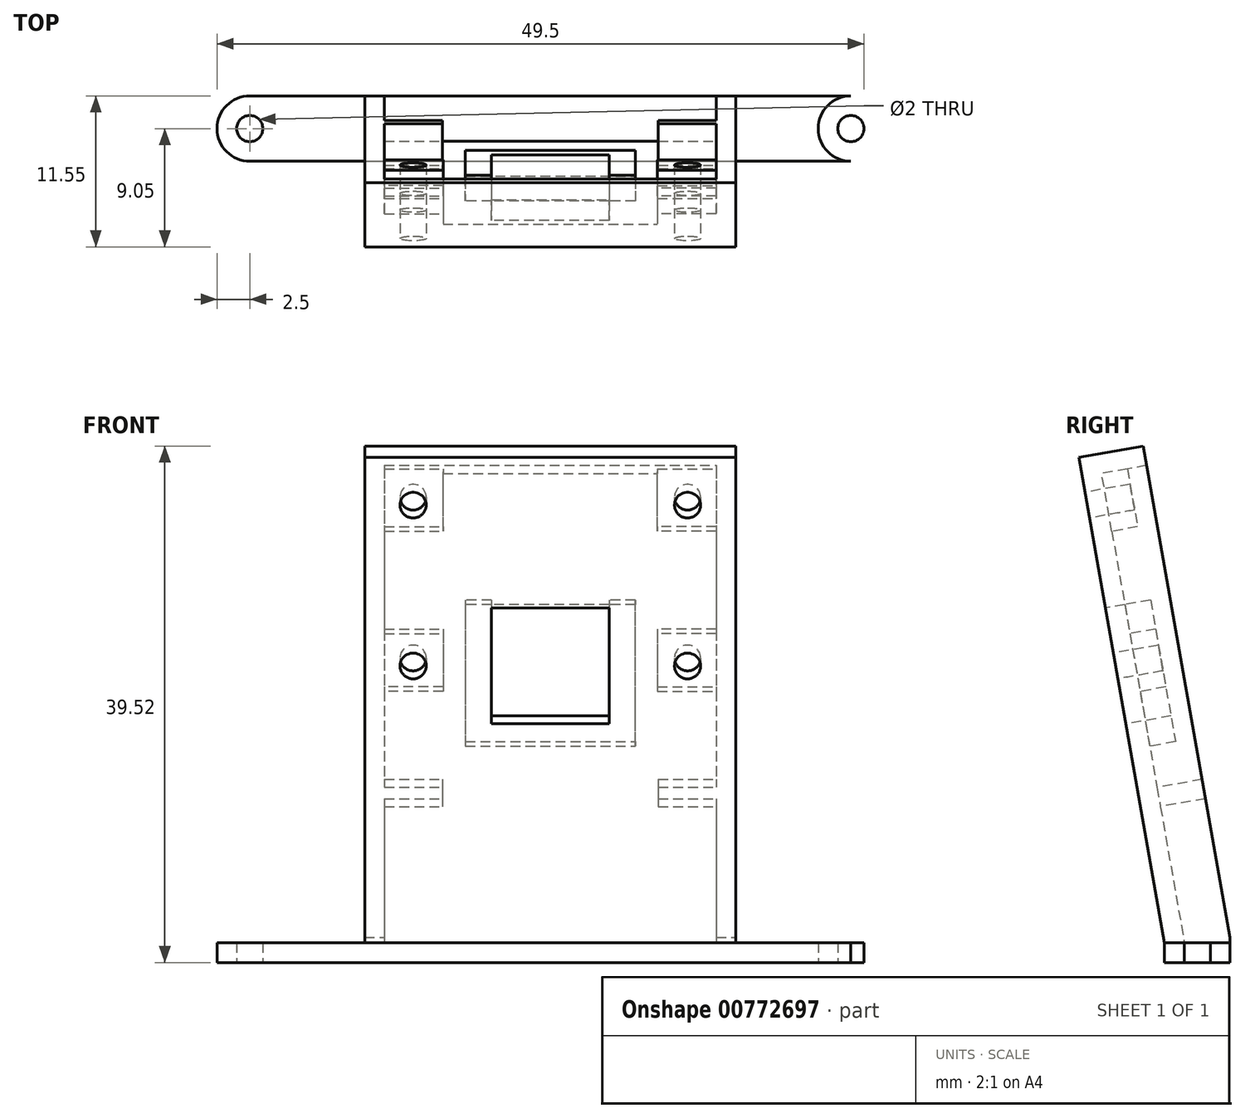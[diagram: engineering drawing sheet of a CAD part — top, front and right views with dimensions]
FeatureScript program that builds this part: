
annotation { "Feature Type Name" : "Feature", "Feature Type Description" : "" }
export const myFeature = defineFeature(function(context is Context, id is Id, definition is map)
    precondition{}
    {
        {
            var Q0;
            Q0=qCreatedBy(makeId("Top.planeOp"),FACE);
            var sketch = newSketch(context, id + "F0", { "sketchPlane" : qUnion([Q0])});
            skLineSegment(sketch, "E0.bottom", {"start": v(-23, 2.5) * mm, "end": v(23, 2.5) * mm});
            skLineSegment(sketch, "E0.top", {"start": v(-23, -2.5) * mm, "end": v(23, -2.5) * mm});
            skCircle(sketch, "E1", {"center": v(-23, 0) * mm, "radius": 2.5 * mm});
            skCircle(sketch, "E2.MirrorC", {"center": v(23, 0) * mm, "radius": 2.5 * mm});
            skCircle(sketch, "E3", {"center": v(-23, 0) * mm, "radius": 1 * mm});
            skCircle(sketch, "E4.MirrorC", {"center": v(23, 0) * mm, "radius": 1 * mm});
            skSolve(sketch);
        }
        {
            var Q0;
            Q0=makeQuery(id+"F0.imprint","IMPRINT",FACE,{"disambiguationData":[TD([[makeQuery(id+"F0.imprint","IMPRINT",EDGE,{"derivedFrom":sQuery(id+"F0.wireOp",EDGE,"E3")}),-1.0]])]});
            var Q1;
            {var subQ0=sQuery(id+"F0.wireOp",EDGE,"E0.bottom");Q1=makeQuery(id+"F0.imprint","IMPRINT",FACE,{"disambiguationData":[TD([[makeQuery(id+"F0.imprint","IMPRINT",EDGE,{"derivedFrom":subQ0}),-1.0]])]});}
            var Q2;
            Q2=makeQuery(id+"F0.imprint","IMPRINT",FACE,{"disambiguationData":[TD([[makeQuery(id+"F0.imprint","IMPRINT",EDGE,{"derivedFrom":sQuery(id+"F0.wireOp",EDGE,"E4.MirrorC")}),1.0]])]});
            extrude(context, id + "F1", {"entities" : qUnion([Q0, Q1, Q2]), "depth" : 1.5 * mm, "offsetDistance" : 25 * mm});
        }
        {
            var Q0;
            Q0=qCreatedBy(makeId("Front.planeOp"),FACE);
            var Q1;
            Q1=makeQuery(id+"F1.opExtrude","CAP_EDGE",EDGE,{"disambiguationData":[OSD([sQuery(id+"F0.wireOp",EDGE,"E0.top")])],"isStart":false});
            cPlane(context, id + "F2", {"entities" : qUnion([Q0, Q1]), "cplaneType" : CPlaneType.LINE_ANGLE, "offset" : 25 * mm, "angle" : 190 * degree, "width" : 150 * mm, "height" : 150 * mm});
        }
        {
            var Q0;
            Q0=qCreatedBy(id+"F2.planeOp",FACE);
            var sketch = newSketch(context, id + "F3", { "sketchPlane" : qUnion([Q0])});
            skLineSegment(sketch, "E5.bottom", {"start": v(-12.5, 37.93) * mm, "end": v(12.5, 37.93) * mm, "construction": true});
            skLineSegment(sketch, "E5.top", {"start": v(-12.5, 13.93) * mm, "end": v(12.5, 13.93) * mm, "construction": true});
            skLineSegment(sketch, "E5.left", {"start": v(-12.5, 37.93) * mm, "end": v(-12.5, 13.93) * mm, "construction": true});
            skLineSegment(sketch, "E5.right", {"start": v(12.5, 37.93) * mm, "end": v(12.5, 13.93) * mm, "construction": true});
            skLineSegment(sketch, "E6.bottom", {"start": v(-4.5, 27.93) * mm, "end": v(4.5, 27.93) * mm});
            skLineSegment(sketch, "E6.top", {"start": v(-4.5, 18.93) * mm, "end": v(4.5, 18.93) * mm});
            skLineSegment(sketch, "E6.left", {"start": v(-4.5, 27.93) * mm, "end": v(-4.5, 18.93) * mm});
            skLineSegment(sketch, "E6.right", {"start": v(4.5, 27.93) * mm, "end": v(4.5, 18.93) * mm});
            skLineSegment(sketch, "E7", {"start": v(-16.59, 23.43) * mm, "end": v(16.18, 23.43) * mm, "construction": true});
            skCircle(sketch, "E8", {"center": v(10.5, 23.43) * mm, "radius": 1 * mm});
            skCircle(sketch, "E9", {"center": v(-10.5, 23.43) * mm, "radius": 1 * mm});
            skCircle(sketch, "E10", {"center": v(-10.5, 35.93) * mm, "radius": 1 * mm});
            skCircle(sketch, "E11", {"center": v(10.5, 35.93) * mm, "radius": 1 * mm});
            skLineSegment(sketch, "E12", {"start": v(-4.5, 27.93) * mm, "end": v(-6.5, 27.93) * mm});
            skLineSegment(sketch, "E13", {"start": v(-6.5, 27.93) * mm, "end": v(-6.5, 16.93) * mm});
            skLineSegment(sketch, "E14", {"start": v(-6.5, 16.93) * mm, "end": v(6.5, 16.93) * mm});
            skLineSegment(sketch, "E15", {"start": v(6.5, 16.93) * mm, "end": v(6.5, 27.93) * mm});
            skLineSegment(sketch, "E16", {"start": v(6.5, 27.93) * mm, "end": v(4.5, 27.93) * mm});
            skLineSegment(sketch, "E17.bottom", {"start": v(-12.7, 38.13) * mm, "end": v(12.7, 38.13) * mm});
            skLineSegment(sketch, "E17.left", {"start": v(-12.7, 38.13) * mm, "end": v(-12.7, 13.73) * mm});
            skLineSegment(sketch, "E17.right", {"start": v(12.7, 38.13) * mm, "end": v(12.7, 13.73) * mm});
            skLineSegment(sketch, "E18.bottom", {"start": v(-14.2, 39.63) * mm, "end": v(14.2, 39.63) * mm});
            skLineSegment(sketch, "E18.left", {"start": v(-14.2, 39.63) * mm, "end": v(-14.2, 0.43) * mm});
            skLineSegment(sketch, "E18.right", {"start": v(14.2, 39.63) * mm, "end": v(14.2, 0.43) * mm});
            skLineSegment(sketch, "E19", {"start": v(-12.7, 13.73) * mm, "end": v(-8.25, 13.73) * mm});
            skLineSegment(sketch, "E20", {"start": v(-12.7, 12.23) * mm, "end": v(-8.25, 12.23) * mm});
            skLineSegment(sketch, "E21.trimOffspring", {"start": v(-12.7, 12.23) * mm, "end": v(-12.7, 0.43) * mm});
            skLineSegment(sketch, "E22.trimOffspring", {"start": v(12.7, 12.23) * mm, "end": v(12.7, 0.43) * mm});
            skLineSegment(sketch, "E23", {"start": v(-12.7, 33.63) * mm, "end": v(-8.2, 33.63) * mm});
            skLineSegment(sketch, "E24", {"start": v(-8.2, 33.63) * mm, "end": v(-8.2, 38.13) * mm});
            skLineSegment(sketch, "E25", {"start": v(-12.7, 25.68) * mm, "end": v(-8.2, 25.68) * mm});
            skLineSegment(sketch, "E26", {"start": v(-8.2, 25.68) * mm, "end": v(-8.2, 21.18) * mm});
            skLineSegment(sketch, "E27", {"start": v(-8.2, 21.18) * mm, "end": v(-12.7, 21.18) * mm});
            skLineSegment(sketch, "E28.MirrorCS", {"start": v(8.2, 33.63) * mm, "end": v(8.2, 38.13) * mm});
            skLineSegment(sketch, "E29.MirrorCS", {"start": v(12.7, 33.63) * mm, "end": v(8.2, 33.63) * mm});
            skLineSegment(sketch, "E30.MirrorCS", {"start": v(8.2, 21.18) * mm, "end": v(12.7, 21.18) * mm});
            skLineSegment(sketch, "E31.MirrorCS", {"start": v(12.7, 25.68) * mm, "end": v(8.2, 25.68) * mm});
            skLineSegment(sketch, "E32.MirrorCS", {"start": v(8.2, 25.68) * mm, "end": v(8.2, 21.18) * mm});
            skLineSegment(sketch, "E33", {"start": v(8.25, 13.73) * mm, "end": v(8.25, 12.23) * mm});
            skLineSegment(sketch, "E34", {"start": v(-8.25, 13.73) * mm, "end": v(-8.25, 12.23) * mm});
            skLineSegment(sketch, "E35.trimOffspring", {"start": v(8.25, 12.23) * mm, "end": v(12.7, 12.23) * mm});
            skLineSegment(sketch, "E36.trimOffspring", {"start": v(8.25, 13.73) * mm, "end": v(12.7, 13.73) * mm});
            skLineSegment(sketch, "E37", {"start": v(-14.2, 0.43) * mm, "end": v(14.2, 0.43) * mm});
            skSolve(sketch);
        }
        {
            var Q0;
            Q0=makeQuery(id+"F3.imprint","IMPRINT",FACE,{"disambiguationData":[TD([[makeQuery(id+"F3.imprint","IMPRINT",EDGE,{"derivedFrom":sQuery(id+"F3.wireOp",EDGE,"E6.bottom")}),1.0]])]});
            extrude(context, id + "F4", {"entities" : qUnion([Q0]), "operationType" : NewBodyOperationType.ADD, "oppositeDirection" : true, "depth" : 1.5 * mm, "offsetDistance" : 25 * mm});
        }
        {
            var Q0;
            Q0=makeQuery(id+"F3.imprint","IMPRINT",FACE,{"disambiguationData":[TD([[makeQuery(id+"F3.imprint","IMPRINT",EDGE,{"derivedFrom":sQuery(id+"F3.wireOp",EDGE,"E18.bottom")}),-1.0]])]});
            extrude(context, id + "F5", {"entities" : qUnion([Q0]), "operationType" : NewBodyOperationType.ADD, "oppositeDirection" : true, "depth" : 5 * mm, "offsetDistance" : 25 * mm});
        }
        {
            var Q0;
            Q0=makeQuery(id+"F3.imprint","IMPRINT",FACE,{"disambiguationData":[TD([[makeQuery(id+"F3.imprint","IMPRINT",EDGE,{"derivedFrom":sQuery(id+"F3.wireOp",EDGE,"E10")}),-1.0]])]});
            var Q1;
            Q1=makeQuery(id+"F3.imprint","IMPRINT",FACE,{"disambiguationData":[TD([[makeQuery(id+"F3.imprint","IMPRINT",EDGE,{"derivedFrom":sQuery(id+"F3.wireOp",EDGE,"E11")}),-1.0]])]});
            var Q2;
            Q2=makeQuery(id+"F3.imprint","IMPRINT",FACE,{"disambiguationData":[TD([[makeQuery(id+"F3.imprint","IMPRINT",EDGE,{"derivedFrom":sQuery(id+"F3.wireOp",EDGE,"E8")}),-1.0]])]});
            var Q3;
            Q3=makeQuery(id+"F3.imprint","IMPRINT",FACE,{"disambiguationData":[TD([[makeQuery(id+"F3.imprint","IMPRINT",EDGE,{"derivedFrom":sQuery(id+"F3.wireOp",EDGE,"E9")}),-1.0]])]});
            var Q4;
            Q4=makeQuery(id+"F3.imprint","IMPRINT",FACE,{"disambiguationData":[TD([[makeQuery(id+"F3.imprint","IMPRINT",EDGE,{"derivedFrom":sQuery(id+"F3.wireOp",EDGE,"E6.top")}),-1.0]])]});
            extrude(context, id + "F6", {"entities" : qUnion([Q0, Q1, Q2, Q3, Q4]), "operationType" : NewBodyOperationType.ADD, "oppositeDirection" : true, "depth" : 3.5 * mm, "offsetDistance" : 25 * mm});
        }
        {
            var Q0;
            Q0=makeQuery(id+"F1.opExtrude","CAP_FACE",FACE,{"disambiguationData":[OSD([sQuery(id+"F0.wireOp",EDGE,"E0.bottom"),sQuery(id+"F0.wireOp",EDGE,"E0.top"),sQuery(id+"F0.wireOp",EDGE,"E1"),sQuery(id+"F0.wireOp",EDGE,"E2.MirrorC"),sQuery(id+"F0.wireOp",EDGE,"E3"),sQuery(id+"F0.wireOp",EDGE,"E4.MirrorC")])],"isStart":true});
            var sketch = newSketch(context, id + "F7", { "sketchPlane" : qUnion([Q0])});
            skLineSegment(sketch, "E38.bottom", {"start": v(-16.8, -2.5) * mm, "end": v(15.78, -2.5) * mm});
            skLineSegment(sketch, "E38.top", {"start": v(-16.8, -5.14) * mm, "end": v(15.78, -5.14) * mm});
            skLineSegment(sketch, "E38.left", {"start": v(-16.8, -2.5) * mm, "end": v(-16.8, -5.14) * mm});
            skLineSegment(sketch, "E38.right", {"start": v(15.78, -2.5) * mm, "end": v(15.78, -5.14) * mm});
            skSolve(sketch);
        }
        {
            var Q0;
            Q0 = qSketchRegion(id + "F7", true);
            extrude(context, id + "F8", {"entities" : qUnion([Q0]), "operationType" : NewBodyOperationType.REMOVE, "oppositeDirection" : true, "depth" : 14.8 * mm, "offsetDistance" : 25 * mm});
        }
    });
